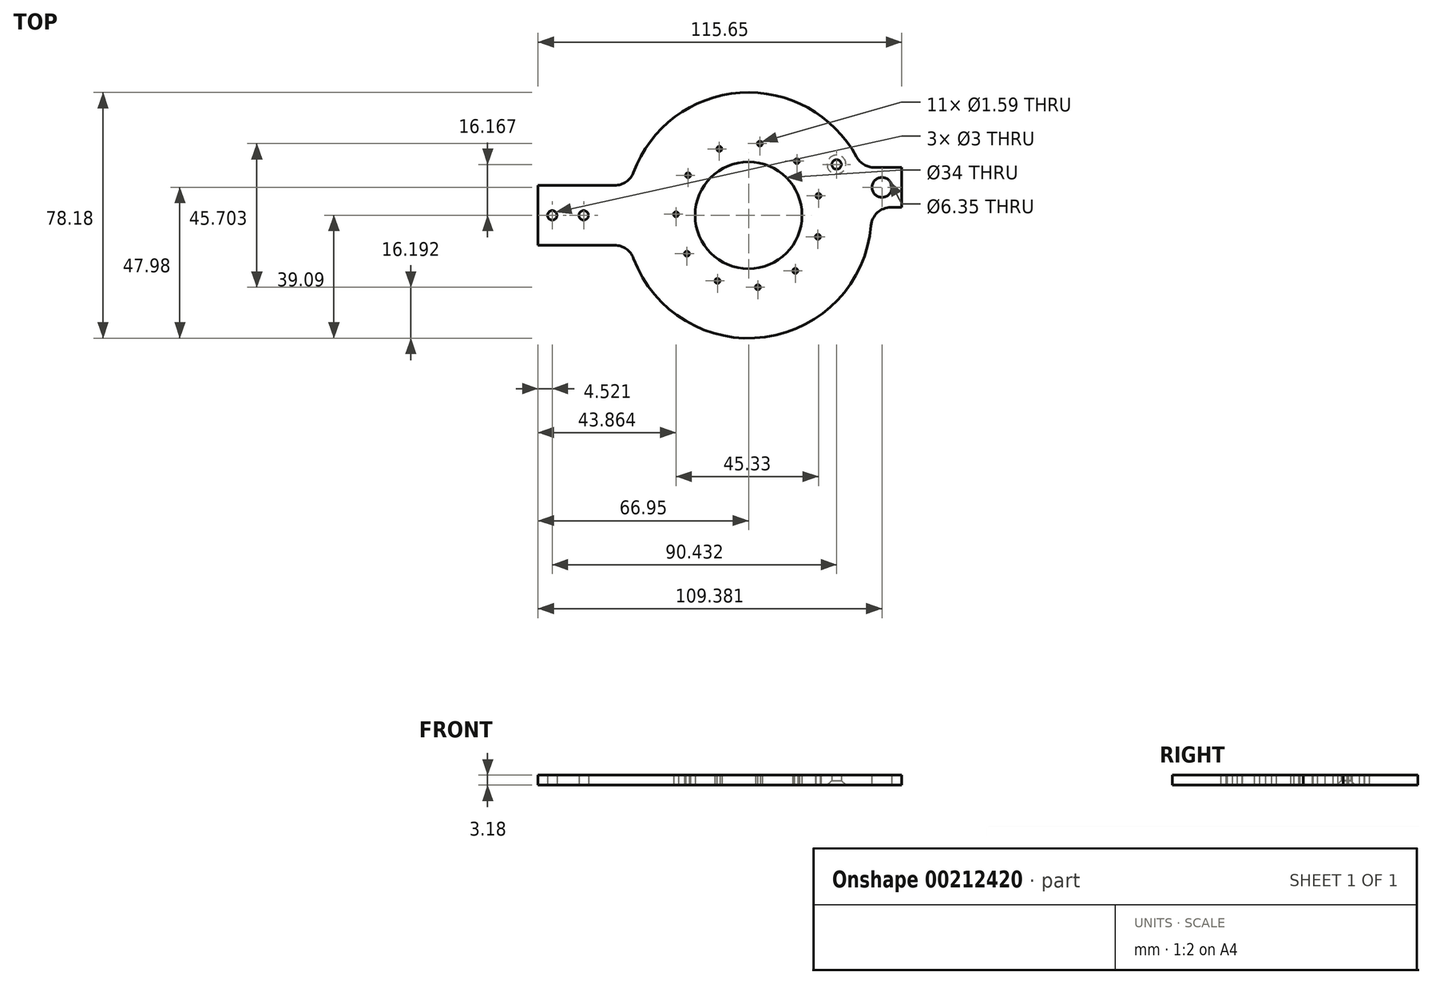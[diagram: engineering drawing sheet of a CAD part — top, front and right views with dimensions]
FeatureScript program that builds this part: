
annotation { "Feature Type Name" : "Feature", "Feature Type Description" : "" }
export const myFeature = defineFeature(function(context is Context, id is Id, definition is map)
    precondition{}
    {
        {
            var Q0;
            Q0=qCreatedBy(makeId("Top.planeOp"),FACE);
            var sketch = newSketch(context, id + "F0", { "sketchPlane" : qUnion([Q0])});
            skCircle(sketch, "E0", {"center": v(0, 0) * mm, "radius": 17 * mm});
            skArc(sketch, "E1", {"start": v(-37.91, -9.52) * mm, "mid": v(6.06, -38.62) * mm, "end": v(39, 2.54) * mm});
            skLineSegment(sketch, "E2.bottom", {"start": v(-37.91, 9.53) * mm, "end": v(-66.95, 9.53) * mm});
            skLineSegment(sketch, "E2.top", {"start": v(-37.91, -9.53) * mm, "end": v(-66.95, -9.52) * mm});
            skLineSegment(sketch, "E2.right", {"start": v(-66.95, 9.52) * mm, "end": v(-66.95, -9.52) * mm});
            skLineSegment(sketch, "E3.bottom", {"start": v(36, 15.24) * mm, "end": v(48.7, 15.24) * mm});
            skLineSegment(sketch, "E3.top", {"start": v(39, 2.54) * mm, "end": v(48.7, 2.54) * mm});
            skLineSegment(sketch, "E3.right", {"start": v(48.7, 15.24) * mm, "end": v(48.7, 2.54) * mm});
            skArc(sketch, "E4.trimOffspring", {"start": v(36, 15.24) * mm, "mid": v(-3.01, 38.97) * mm, "end": v(-37.91, 9.52) * mm});
            skSolve(sketch);
        }
        {
            var Q0;
            Q0=makeQuery(id+"F0.imprint","IMPRINT",FACE,{"disambiguationData":[TD([[makeQuery(id+"F0.imprint","IMPRINT",EDGE,{"derivedFrom":sQuery(id+"F0.wireOp",EDGE,"E0")}),-1.0]])]});
            extrude(context, id + "F1", {"entities" : qUnion([Q0]), "depth" : 3.17 * mm});
        }
        {
            var Q0;
            Q0=makeQuery(id+"F1.opExtrude","CAP_FACE",FACE,{"disambiguationData":[OSD([sQuery(id+"F0.wireOp",EDGE,"E0"),sQuery(id+"F0.wireOp",EDGE,"E1")])],"isStart":false});
            var sketch = newSketch(context, id + "F2", { "sketchPlane" : qUnion([Q0])});
            skCircle(sketch, "E5", {"center": v(3.61, 22.8) * mm, "radius": 0.8 * mm});
            skLineSegment(sketch, "E6", {"start": v(0, 0) * mm, "end": v(3.61, 22.8) * mm, "construction": true});
            skSolve(sketch);
        }
        {
            var Q0;
            Q0 = qSketchRegion(id + "F2", true);
            extrude(context, id + "F3", {"entities" : qUnion([Q0]), "endBound" : BoundingType.SYMMETRIC, "depth" : 25.4 * mm});
        }
        {
            var Q0;
            Q0=makeQuery(id+"F3.opExtrude","SWEPT_BODY",BODY,{"disambiguationData":[OSD([sQuery(id+"F2.wireOp",EDGE,"E5")])]});
            var Q1;
            Q1=makeQuery(id+"F1.opExtrude","SWEPT_FACE",FACE,{"disambiguationData":[OSD([sQuery(id+"F0.wireOp",EDGE,"E0")])]});
            circularPattern(context, id + "F4", {"operationType" : NewBodyOperationType.REMOVE, "entities" : qUnion([Q0]), "axis" : qUnion([Q1]), "angle" : 360 * degree, "instanceCount" : 11, "equalSpace" : true});
        }
        {
            var Q0;
            Q0=qCreatedBy(makeId("Top.planeOp"),FACE);
            var sketch = newSketch(context, id + "F5", { "sketchPlane" : qUnion([Q0])});
            skLineSegment(sketch, "E7", {"start": v(0, 0) * mm, "end": v(28, 16.17) * mm});
            skSolve(sketch);
        }
        {
            var Q0;
            Q0=sQuery(id+"F5.wireOp",VERTEX,"E7.end");
            var Q1;
            Q1=makeQuery(id+"F1.opExtrude","SWEPT_BODY",BODY,{"disambiguationData":[OSD([sQuery(id+"F0.wireOp",EDGE,"E0"),sQuery(id+"F0.wireOp",EDGE,"E1"),sQuery(id+"F0.wireOp",EDGE,"E2.bottom"),sQuery(id+"F0.wireOp",EDGE,"E2.top"),sQuery(id+"F0.wireOp",EDGE,"E2.right"),sQuery(id+"F0.wireOp",EDGE,"E3.bottom"),sQuery(id+"F0.wireOp",EDGE,"E3.top"),sQuery(id+"F0.wireOp",EDGE,"E3.right"),sQuery(id+"F0.wireOp",EDGE,"E4.trimOffspring")])]});
            hole(context, id + "F6", {"style" : HoleStyle.C_SINK, "endStyle" : HoleEndStyle.THROUGH, "oppositeDirection" : true, "holeDiameter" : 3 * mm, "cSinkDiameter" : 6 * mm, "cSinkAngle" : 90 * degree, "locations" : qUnion([Q0]), "scope" : qUnion([Q1]), "isTappedThrough" : true});
        }
        {
            var Q0;
            Q0=qCreatedBy(makeId("Top.planeOp"),FACE);
            var sketch = newSketch(context, id + "F7", { "sketchPlane" : qUnion([Q0])});
            skLineSegment(sketch, "E8", {"start": v(-62.43, 0) * mm, "end": v(-52.43, 0) * mm});
            skLineSegment(sketch, "E9", {"start": v(-57.43, 0) * mm, "end": v(-57.43, 9.53) * mm, "construction": true});
            skSolve(sketch);
        }
        {
            var Q0;
            Q0=sQuery(id+"F7.wireOp",VERTEX,"E8.start");
            var Q1;
            Q1=sQuery(id+"F7.wireOp",VERTEX,"E8.end");
            var Q2;
            Q2=makeQuery(id+"F1.opExtrude","SWEPT_BODY",BODY,{"disambiguationData":[OSD([sQuery(id+"F0.wireOp",EDGE,"E0"),sQuery(id+"F0.wireOp",EDGE,"E1"),sQuery(id+"F0.wireOp",EDGE,"E2.bottom"),sQuery(id+"F0.wireOp",EDGE,"E2.top"),sQuery(id+"F0.wireOp",EDGE,"E2.right"),sQuery(id+"F0.wireOp",EDGE,"E3.bottom"),sQuery(id+"F0.wireOp",EDGE,"E3.top"),sQuery(id+"F0.wireOp",EDGE,"E3.right"),sQuery(id+"F0.wireOp",EDGE,"E4.trimOffspring")])]});
            hole(context, id + "F8", {"style" : HoleStyle.SIMPLE, "endStyle" : HoleEndStyle.THROUGH, "oppositeDirection" : true, "holeDiameter" : 3 * mm, "locations" : qUnion([Q0, Q1]), "scope" : qUnion([Q2]), "isTappedThrough" : true});
        }
        {
            var Q0;
            Q0=makeQuery(id+"F1.opExtrude","CAP_FACE",FACE,{"disambiguationData":[OSD([sQuery(id+"F0.wireOp",EDGE,"E0"),sQuery(id+"F0.wireOp",EDGE,"E1"),sQuery(id+"F0.wireOp",EDGE,"E2.bottom"),sQuery(id+"F0.wireOp",EDGE,"E2.top"),sQuery(id+"F0.wireOp",EDGE,"E2.right"),sQuery(id+"F0.wireOp",EDGE,"E3.bottom"),sQuery(id+"F0.wireOp",EDGE,"E3.top"),sQuery(id+"F0.wireOp",EDGE,"E3.right"),sQuery(id+"F0.wireOp",EDGE,"E4.trimOffspring")])],"isStart":false});
            var sketch = newSketch(context, id + "F9", { "sketchPlane" : qUnion([Q0])});
            skPoint(sketch, "E10", {"position": v(42.43, 8.9) * mm});
            skLineSegment(sketch, "E11", {"start": v(42.43, 8.9) * mm, "end": v(48.7, 8.9) * mm, "construction": true});
            skSolve(sketch);
        }
        {
            var Q0;
            Q0=sQuery(id+"F9.wireOp",VERTEX,"E10");
            var Q1;
            Q1=makeQuery(id+"F1.opExtrude","SWEPT_BODY",BODY,{"disambiguationData":[OSD([sQuery(id+"F0.wireOp",EDGE,"E0"),sQuery(id+"F0.wireOp",EDGE,"E1"),sQuery(id+"F0.wireOp",EDGE,"E2.bottom"),sQuery(id+"F0.wireOp",EDGE,"E2.top"),sQuery(id+"F0.wireOp",EDGE,"E2.right"),sQuery(id+"F0.wireOp",EDGE,"E3.bottom"),sQuery(id+"F0.wireOp",EDGE,"E3.top"),sQuery(id+"F0.wireOp",EDGE,"E3.right"),sQuery(id+"F0.wireOp",EDGE,"E4.trimOffspring")])]});
            hole(context, id + "F10", {"style" : HoleStyle.SIMPLE, "endStyle" : HoleEndStyle.THROUGH, "holeDiameter" : 6.35 * mm, "locations" : qUnion([Q0]), "scope" : qUnion([Q1]), "isTappedThrough" : true});
        }
        {
            var Q0;
            Q0=makeQuery(id+"F1.opExtrude","SWEPT_EDGE",EDGE,{"disambiguationData":[OSD([sQuery(id+"F0.wireOp",EDGE,"E2.bottom"),sQuery(id+"F0.wireOp",EDGE,"E4.trimOffspring")])]});
            var Q1;
            Q1=makeQuery(id+"F1.opExtrude","SWEPT_EDGE",EDGE,{"disambiguationData":[OSD([sQuery(id+"F0.wireOp",EDGE,"E1"),sQuery(id+"F0.wireOp",EDGE,"E2.top")])]});
            var Q2;
            Q2=makeQuery(id+"F1.opExtrude","SWEPT_EDGE",EDGE,{"disambiguationData":[OSD([sQuery(id+"F0.wireOp",EDGE,"E1"),sQuery(id+"F0.wireOp",EDGE,"E3.top")])]});
            var Q3;
            Q3=makeQuery(id+"F1.opExtrude","SWEPT_EDGE",EDGE,{"disambiguationData":[OSD([sQuery(id+"F0.wireOp",EDGE,"E3.bottom"),sQuery(id+"F0.wireOp",EDGE,"E4.trimOffspring")])]});
            fillet(context, id + "F11", {"entities" : qUnion([Q0, Q1, Q2, Q3]), "radius" : 6.35 * mm, "tangentPropagation" : true, "allowEdgeOverflow" : false});
        }
    });
